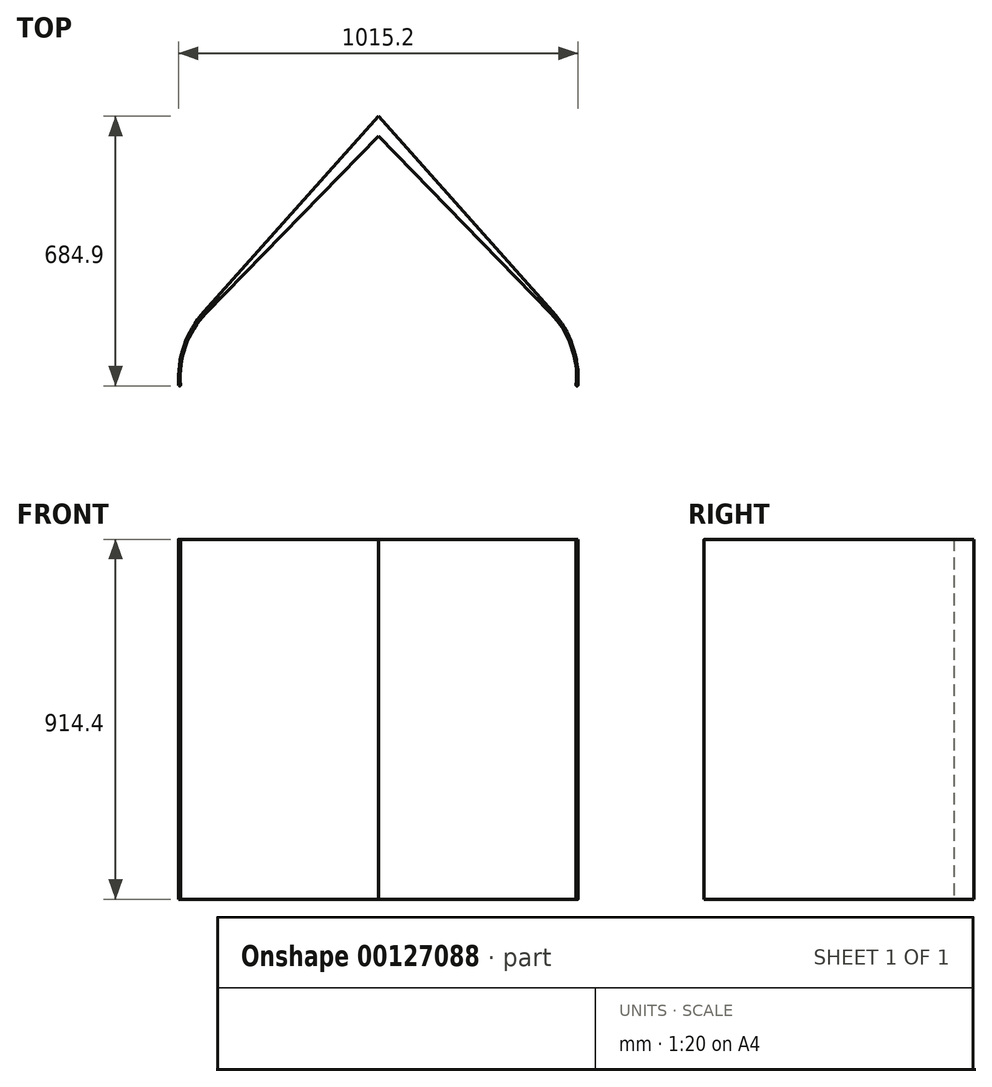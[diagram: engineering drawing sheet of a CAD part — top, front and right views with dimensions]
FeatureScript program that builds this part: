
annotation { "Feature Type Name" : "Feature", "Feature Type Description" : "" }
export const myFeature = defineFeature(function(context is Context, id is Id, definition is map)
    precondition{}
    {
        {
            var Q0;
            Q0=qCreatedBy(makeId("Top.planeOp"),FACE);
            var sketch = newSketch(context, id + "F0", { "sketchPlane" : qUnion([Q0])});
            skLineSegment(sketch, "E0", {"start": v(0, 0) * mm, "end": v(0, -762) * mm, "construction": true});
            skLineSegment(sketch, "E1", {"start": v(0, 0) * mm, "end": v(442.88, -496.59) * mm});
            skArc(sketch, "E2", {"start": v(442.88, -496.59) * mm, "mid": v(493.66, -583.23) * mm, "end": v(507.08, -682.76) * mm});
            skLineSegment(sketch, "E3.trimOffspring", {"start": v(0, -50.8) * mm, "end": v(437.83, -500.45) * mm});
            skArc(sketch, "E4", {"start": v(437.83, -500.45) * mm, "mid": v(490.07, -584.36) * mm, "end": v(502.52, -682.4) * mm});
            skArc(sketch, "E5", {"start": v(502.52, -682.4) * mm, "mid": v(504.62, -684.9) * mm, "end": v(507.08, -682.76) * mm});
            skArc(sketch, "E6.MirrorCS", {"start": v(-502.52, -682.4) * mm, "mid": v(-504.62, -684.9) * mm, "end": v(-507.08, -682.76) * mm});
            skArc(sketch, "E7.MirrorCS", {"start": v(-442.88, -496.59) * mm, "mid": v(-493.66, -583.23) * mm, "end": v(-507.08, -682.76) * mm});
            skArc(sketch, "E8.MirrorCS", {"start": v(-437.83, -500.45) * mm, "mid": v(-490.07, -584.36) * mm, "end": v(-502.52, -682.4) * mm});
            skLineSegment(sketch, "E9.MirrorCS", {"start": v(0, 0) * mm, "end": v(-442.88, -496.59) * mm});
            skLineSegment(sketch, "E10.MirrorCS", {"start": v(0, -50.8) * mm, "end": v(-437.83, -500.45) * mm});
            skSolve(sketch);
        }
        {
            var Q0;
            Q0=makeQuery(id+"F0.imprint","IMPRINT",FACE,{"disambiguationData":[TD([[makeQuery(id+"F0.imprint","IMPRINT",EDGE,{"derivedFrom":sQuery(id+"F0.wireOp",EDGE,"E1")}),-1.0]])]});
            extrude(context, id + "F1", {"entities" : qUnion([Q0]), "depth" : 914.4 * mm, "offsetDistance" : 25.4 * mm});
        }
    });
